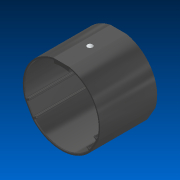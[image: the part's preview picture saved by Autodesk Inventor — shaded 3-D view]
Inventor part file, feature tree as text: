
AUTODESK INVENTOR PART (.ipt)
format: ipt  version: 2022.2 (Build 262287000, 287)  size: 222,720 bytes
history: native  units: in
note: dims shown in document units (in); Inventor stores cm internally (conversion verified against a paired STEP export)
features: chamfer x1
ambient origin geometry x8: Origin, YZ Plane, XZ Plane, XY Plane, X Axis, Y Axis, Z Axis, Center Point
bodies: Solid1 (feature_tree)
feature tree (1):
  chamfer  "Chamfer1"  [1 undecoded]
note: 1 required parameter value undecoded (feature->parameter linkage not recoverable at this tier; creation-order binding heuristic only, values carry confidence <= 0.55)
